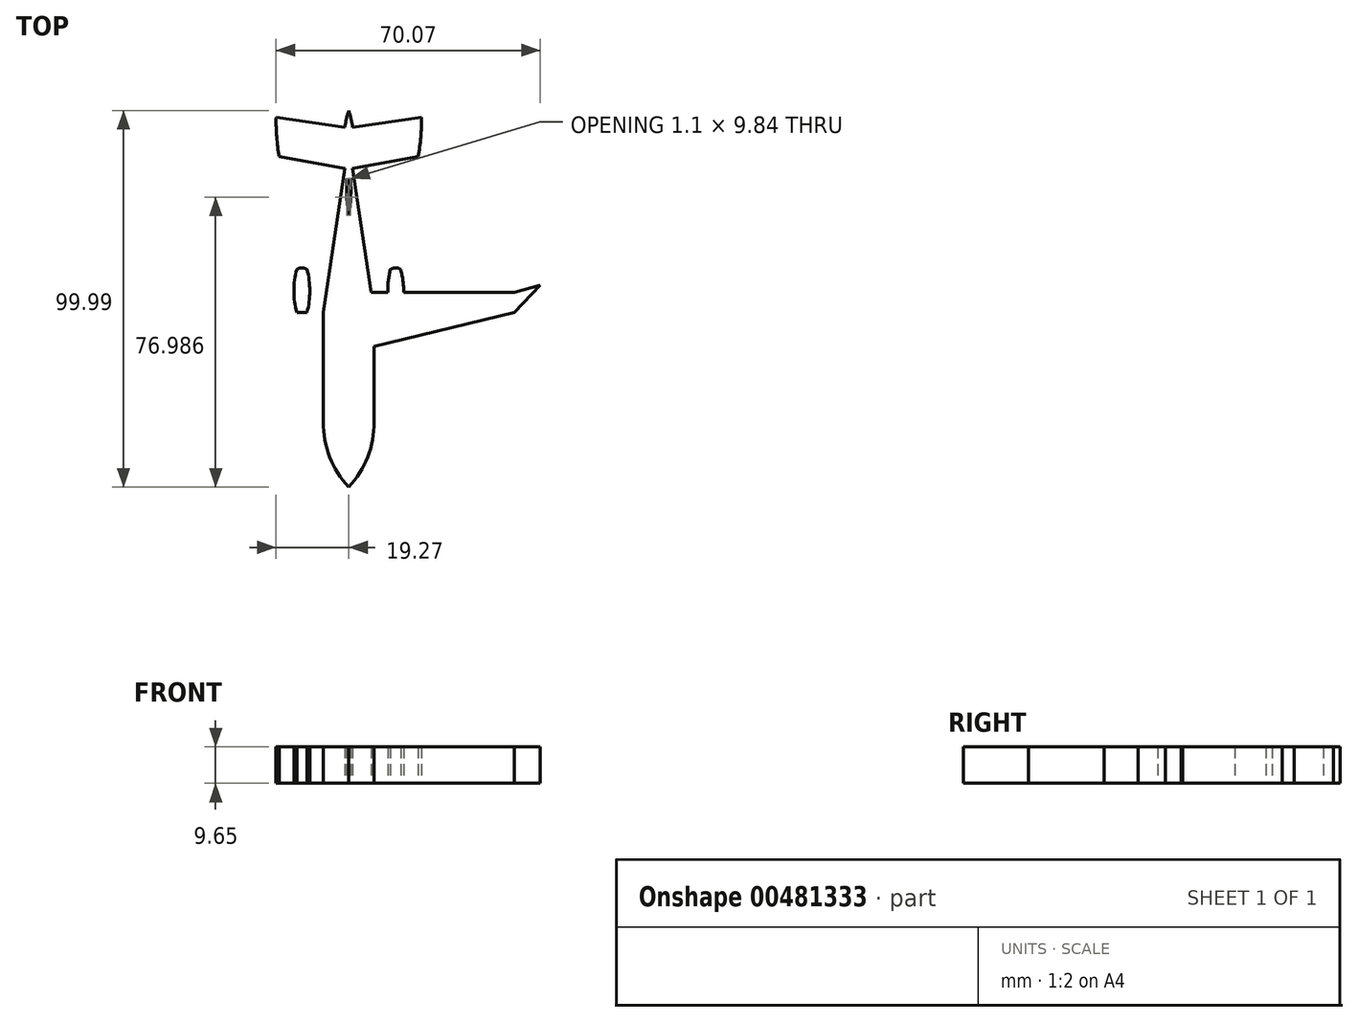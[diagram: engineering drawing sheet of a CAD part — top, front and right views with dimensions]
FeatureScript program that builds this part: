
annotation { "Feature Type Name" : "Feature", "Feature Type Description" : "" }
export const myFeature = defineFeature(function(context is Context, id is Id, definition is map)
    precondition{}
    {
        {
            var Q0;
            Q0=qCreatedBy(makeId("Top.planeOp"),FACE);
            var sketch = newSketch(context, id + "F0", { "sketchPlane" : qUnion([Q0])});
            skLineSegment(sketch, "E0", {"start": v(0, 0) * mm, "end": v(0, 53.58) * mm, "construction": true});
            skLineSegment(sketch, "E1", {"start": v(0, 0) * mm, "end": v(50.8, 0) * mm, "construction": true});
            skLineSegment(sketch, "E2", {"start": v(50.8, 0) * mm, "end": v(50.8, 53.49) * mm, "construction": true});
            skLineSegment(sketch, "E3", {"start": v(50.8, 53.49) * mm, "end": v(0, 53.58) * mm, "construction": true});
            skLineSegment(sketch, "E4", {"start": v(0, 0) * mm, "end": v(-50.8, 0) * mm, "construction": true});
            skLineSegment(sketch, "E5", {"start": v(-50.8, 0) * mm, "end": v(-50.8, 53.57) * mm, "construction": true});
            skLineSegment(sketch, "E6", {"start": v(-50.8, 53.57) * mm, "end": v(0, 53.57) * mm, "construction": true});
            skLineSegment(sketch, "E7.MirrorCS", {"start": v(-50.8, -53.57) * mm, "end": v(0, -53.57) * mm, "construction": true});
            skLineSegment(sketch, "E8.MirrorCS", {"start": v(-50.8, 0) * mm, "end": v(-50.8, -53.57) * mm, "construction": true});
            skLineSegment(sketch, "E9.MirrorCS", {"start": v(50.8, 0) * mm, "end": v(50.8, -53.49) * mm, "construction": true});
            skLineSegment(sketch, "E10.MirrorCS", {"start": v(50.8, -53.49) * mm, "end": v(0, -53.58) * mm, "construction": true});
            skLineSegment(sketch, "E11.bottom", {"start": v(-50.8, 53.57) * mm, "end": v(50.8, 53.57) * mm, "construction": true});
            skLineSegment(sketch, "E11.right", {"start": v(50.8, 53.57) * mm, "end": v(50.8, -53.49) * mm, "construction": true});
            skLineSegment(sketch, "E12", {"start": v(0, 0) * mm, "end": v(50.8, 53.57) * mm, "construction": true});
            skLineSegment(sketch, "E13", {"start": v(0, 0) * mm, "end": v(-50.8, 53.57) * mm, "construction": true});
            skLineSegment(sketch, "E14", {"start": v(0, 0) * mm, "end": v(-50.8, -53.57) * mm, "construction": true});
            skLineSegment(sketch, "E15", {"start": v(0, 0) * mm, "end": v(50.8, -53.49) * mm, "construction": true});
            skLineSegment(sketch, "E16", {"start": v(0, 53.58) * mm, "end": v(-50.8, 0) * mm, "construction": true});
            skLineSegment(sketch, "E17", {"start": v(-50.8, 0) * mm, "end": v(0, -53.57) * mm, "construction": true});
            skLineSegment(sketch, "E18", {"start": v(0, -53.57) * mm, "end": v(50.8, 0) * mm, "construction": true});
            skLineSegment(sketch, "E19", {"start": v(50.8, 0) * mm, "end": v(0, 53.58) * mm, "construction": true});
            skLineSegment(sketch, "E20", {"start": v(-25.4, 26.79) * mm, "end": v(25.4, 26.79) * mm, "construction": true});
            skLineSegment(sketch, "E21", {"start": v(25.4, -26.74) * mm, "end": v(25.4, 26.79) * mm, "construction": true});
            skLineSegment(sketch, "E22", {"start": v(25.4, -26.74) * mm, "end": v(-25.36, -26.74) * mm, "construction": true});
            skLineSegment(sketch, "E23", {"start": v(-25.36, -26.74) * mm, "end": v(-25.4, 26.79) * mm, "construction": true});
            skLineSegment(sketch, "E24", {"start": v(-25.4, 26.79) * mm, "end": v(-25.4, 53.58) * mm, "construction": true});
            skLineSegment(sketch, "E25", {"start": v(-25.36, -26.74) * mm, "end": v(-25.34, -53.57) * mm, "construction": true});
            skLineSegment(sketch, "E26", {"start": v(-25.4, 26.79) * mm, "end": v(-50.8, 26.77) * mm, "construction": true});
            skLineSegment(sketch, "E27", {"start": v(-25.36, -26.74) * mm, "end": v(-50.8, -26.74) * mm, "construction": true});
            skLineSegment(sketch, "E28", {"start": v(25.4, -26.74) * mm, "end": v(25.45, -53.53) * mm, "construction": true});
            skLineSegment(sketch, "E29", {"start": v(25.4, 26.79) * mm, "end": v(25.4, 53.57) * mm, "construction": true});
            skLineSegment(sketch, "E30", {"start": v(25.4, -26.74) * mm, "end": v(50.8, -26.7) * mm, "construction": true});
            skLineSegment(sketch, "E31", {"start": v(25.4, 26.79) * mm, "end": v(50.8, 26.79) * mm, "construction": true});
            skCircle(sketch, "E32", {"center": v(0, 0) * mm, "radius": 36.92 * mm, "construction": true});
            skCircle(sketch, "E33", {"center": v(-25.4, 26.79) * mm, "radius": 26.8 * mm, "construction": true});
            skCircle(sketch, "E34", {"center": v(-25.36, -26.74) * mm, "radius": 26.74 * mm, "construction": true});
            skCircle(sketch, "E35", {"center": v(25.4, -26.74) * mm, "radius": 26.74 * mm, "construction": true});
            skCircle(sketch, "E36", {"center": v(25.4, 26.79) * mm, "radius": 26.74 * mm, "construction": true});
            skCircle(sketch, "E37", {"center": v(0, 0) * mm, "radius": 26.79 * mm, "construction": true});
            skCircle(sketch, "E38", {"center": v(0, 0) * mm, "radius": 9.84 * mm, "construction": true});
            skCircle(sketch, "E39", {"center": v(-25.4, 26.79) * mm, "radius": 10.13 * mm, "construction": true});
            skCircle(sketch, "E40", {"center": v(-25.4, 26.79) * mm, "radius": 18.83 * mm, "construction": true});
            skCircle(sketch, "E41.MirrorC", {"center": v(25.4, 26.79) * mm, "radius": 10.13 * mm, "construction": true});
            skCircle(sketch, "E42.MirrorC", {"center": v(25.4, 26.79) * mm, "radius": 18.83 * mm, "construction": true});
            skCircle(sketch, "E43.MirrorC", {"center": v(-25.4, -26.79) * mm, "radius": 18.83 * mm, "construction": true});
            skCircle(sketch, "E44.MirrorC", {"center": v(-25.4, -26.79) * mm, "radius": 10.13 * mm, "construction": true});
            skCircle(sketch, "E45.MirrorC", {"center": v(25.4, -26.79) * mm, "radius": 18.83 * mm, "construction": true});
            skCircle(sketch, "E46.MirrorC", {"center": v(25.4, -26.79) * mm, "radius": 10.13 * mm, "construction": true});
            skLineSegment(sketch, "E47", {"start": v(-25.4, 53.58) * mm, "end": v(-50.8, 26.77) * mm, "construction": true});
            skLineSegment(sketch, "E48", {"start": v(-50.8, 26.77) * mm, "end": v(-25.38, 0) * mm, "construction": true});
            skLineSegment(sketch, "E49", {"start": v(-25.38, 0) * mm, "end": v(-50.8, -26.74) * mm, "construction": true});
            skLineSegment(sketch, "E50", {"start": v(-50.8, -26.74) * mm, "end": v(-25.34, -53.57) * mm, "construction": true});
            skLineSegment(sketch, "E51", {"start": v(0, 0) * mm, "end": v(0, -53.57) * mm, "construction": true});
            skLineSegment(sketch, "E52", {"start": v(-25.34, -53.57) * mm, "end": v(0, -26.79) * mm, "construction": true});
            skLineSegment(sketch, "E53", {"start": v(-25.38, 0) * mm, "end": v(0, -26.79) * mm, "construction": true});
            skLineSegment(sketch, "E54", {"start": v(-25.38, 0) * mm, "end": v(0, 26.76) * mm, "construction": true});
            skLineSegment(sketch, "E55", {"start": v(0, 26.76) * mm, "end": v(-25.4, 53.58) * mm, "construction": true});
            skLineSegment(sketch, "E56", {"start": v(25.4, 53.57) * mm, "end": v(0, 26.76) * mm, "construction": true});
            skLineSegment(sketch, "E57", {"start": v(0, 26.76) * mm, "end": v(25.4, 0.04) * mm, "construction": true});
            skLineSegment(sketch, "E58", {"start": v(0, -26.79) * mm, "end": v(25.4, 0.04) * mm, "construction": true});
            skLineSegment(sketch, "E59", {"start": v(25.45, -53.53) * mm, "end": v(0, -26.79) * mm, "construction": true});
            skLineSegment(sketch, "E60", {"start": v(25.45, -53.53) * mm, "end": v(50.8, -26.7) * mm, "construction": true});
            skLineSegment(sketch, "E61", {"start": v(25.4, 0.04) * mm, "end": v(50.8, -26.7) * mm, "construction": true});
            skLineSegment(sketch, "E62", {"start": v(50.8, 26.79) * mm, "end": v(25.4, 0.04) * mm, "construction": true});
            skLineSegment(sketch, "E63", {"start": v(50.8, 26.79) * mm, "end": v(25.4, 53.57) * mm, "construction": true});
            skArc(sketch, "E64", {"start": v(-6.7, -36.3) * mm, "mid": v(-5.05, -45.6) * mm, "end": v(0, -53.57) * mm});
            skLineSegment(sketch, "E65", {"start": v(-6.7, -36.3) * mm, "end": v(-6.7, -7.21) * mm});
            skLineSegment(sketch, "E66", {"start": v(50.8, 31) * mm, "end": v(-50.8, 31) * mm, "construction": true});
            skLineSegment(sketch, "E67", {"start": v(-6.7, -7.21) * mm, "end": v(-1.01, 31) * mm});
            skArc(sketch, "E68", {"start": v(0, 46.42) * mm, "mid": v(-1.48, 36.59) * mm, "end": v(0, 26.76) * mm});
            skLineSegment(sketch, "E69", {"start": v(-1.01, 31) * mm, "end": v(-18.43, 34.14) * mm});
            skArc(sketch, "E70", {"start": v(-19.26, 44.59) * mm, "mid": v(-19.12, 39.34) * mm, "end": v(-18.43, 34.14) * mm});
            skLineSegment(sketch, "E71", {"start": v(-19.26, 44.59) * mm, "end": v(-1.05, 41.97) * mm});
            skArc(sketch, "E72.MirrorCS", {"start": v(6.7, -36.3) * mm, "mid": v(5.05, -45.6) * mm, "end": v(0, -53.57) * mm});
            skLineSegment(sketch, "E73.MirrorCS", {"start": v(6.7, -36.3) * mm, "end": v(6.7, -7.21) * mm});
            skLineSegment(sketch, "E74.MirrorCS", {"start": v(6.7, -7.21) * mm, "end": v(1.01, 31) * mm});
            skArc(sketch, "E75.MirrorCS", {"start": v(0, 46.42) * mm, "mid": v(1.48, 36.59) * mm, "end": v(0, 26.76) * mm});
            skLineSegment(sketch, "E76.MirrorCS", {"start": v(19.26, 44.59) * mm, "end": v(1.05, 41.97) * mm});
            skArc(sketch, "E77.MirrorCS", {"start": v(19.26, 44.59) * mm, "mid": v(19.12, 39.34) * mm, "end": v(18.43, 34.14) * mm});
            skLineSegment(sketch, "E78.MirrorCS", {"start": v(1.01, 31) * mm, "end": v(18.43, 34.14) * mm});
            skLineSegment(sketch, "E79", {"start": v(50.8, 28.34) * mm, "end": v(-50.8, 28.34) * mm, "construction": true});
            skArc(sketch, "E80", {"start": v(-0.44, 28.34) * mm, "mid": v(-0.51, 23.33) * mm, "end": v(0.02, 18.35) * mm});
            skArc(sketch, "E81.MirrorCS", {"start": v(0.44, 28.34) * mm, "mid": v(0.51, 23.33) * mm, "end": v(-0.02, 18.35) * mm});
            skLineSegment(sketch, "E82", {"start": v(6.7, -16.21) * mm, "end": v(43.96, -7.21) * mm});
            skLineSegment(sketch, "E83", {"start": v(43.96, -7.21) * mm, "end": v(50.8, 0) * mm});
            skLineSegment(sketch, "E84", {"start": v(50.8, 0) * mm, "end": v(43.96, -1.94) * mm});
            skLineSegment(sketch, "E85", {"start": v(13.77, -14.5) * mm, "end": v(13.77, 22.98) * mm, "construction": true});
            skArc(sketch, "E86", {"start": v(13.77, -7.21) * mm, "mid": v(14.56, -1.49) * mm, "end": v(13.77, 4.24) * mm});
            skLineSegment(sketch, "E87", {"start": v(13.77, -7.21) * mm, "end": v(11.05, -7.21) * mm});
            skArc(sketch, "E88", {"start": v(11.05, 4.22) * mm, "mid": v(10.33, -1.5) * mm, "end": v(11.05, -7.21) * mm});
            skArc(sketch, "E89", {"start": v(13.77, 4.24) * mm, "mid": v(12.41, 4.62) * mm, "end": v(11.05, 4.22) * mm});
            skLineSegment(sketch, "E90", {"start": v(43.96, -1.94) * mm, "end": v(14.55, -1.94) * mm});
            skLineSegment(sketch, "E91", {"start": v(10.34, -1.94) * mm, "end": v(5.92, -1.94) * mm});
            skLineSegment(sketch, "E92.MirrorCS", {"start": v(0, -53.57) * mm, "end": v(-50.8, 0) * mm, "construction": true});
            skLineSegment(sketch, "E93.MirrorCS", {"start": v(-50.8, 0) * mm, "end": v(-43.96, -1.94) * mm});
            skArc(sketch, "E94.MirrorCS", {"start": v(-13.77, -7.21) * mm, "mid": v(-14.56, -1.49) * mm, "end": v(-13.77, 4.24) * mm});
            skArc(sketch, "E95.MirrorCS", {"start": v(-11.05, 4.22) * mm, "mid": v(-10.33, -1.5) * mm, "end": v(-11.05, -7.21) * mm});
            skLineSegment(sketch, "E96.MirrorCS", {"start": v(-6.7, -7.21) * mm, "end": v(-50.8, -7.21) * mm, "construction": true});
            skLineSegment(sketch, "E97.MirrorCS", {"start": v(-13.77, -7.21) * mm, "end": v(-11.05, -7.21) * mm});
            skArc(sketch, "E98.MirrorCS", {"start": v(-13.77, 4.24) * mm, "mid": v(-12.41, 4.62) * mm, "end": v(-11.05, 4.22) * mm});
            skLineSegment(sketch, "E99.MirrorCS", {"start": v(-10.34, -1.94) * mm, "end": v(-5.92, -1.94) * mm});
            skLineSegment(sketch, "E100.MirrorCS", {"start": v(-6.7, -16.21) * mm, "end": v(-43.96, -7.21) * mm});
            skLineSegment(sketch, "E101.MirrorCS", {"start": v(-43.96, -1.94) * mm, "end": v(-14.55, -1.94) * mm});
            skSolve(sketch);
        }
        {
            var Q0;
            Q0 = qSketchRegion(id + "F0", true);
            extrude(context, id + "F1", {"entities" : qUnion([Q0]), "depth" : 9.65 * mm});
        }
    });
